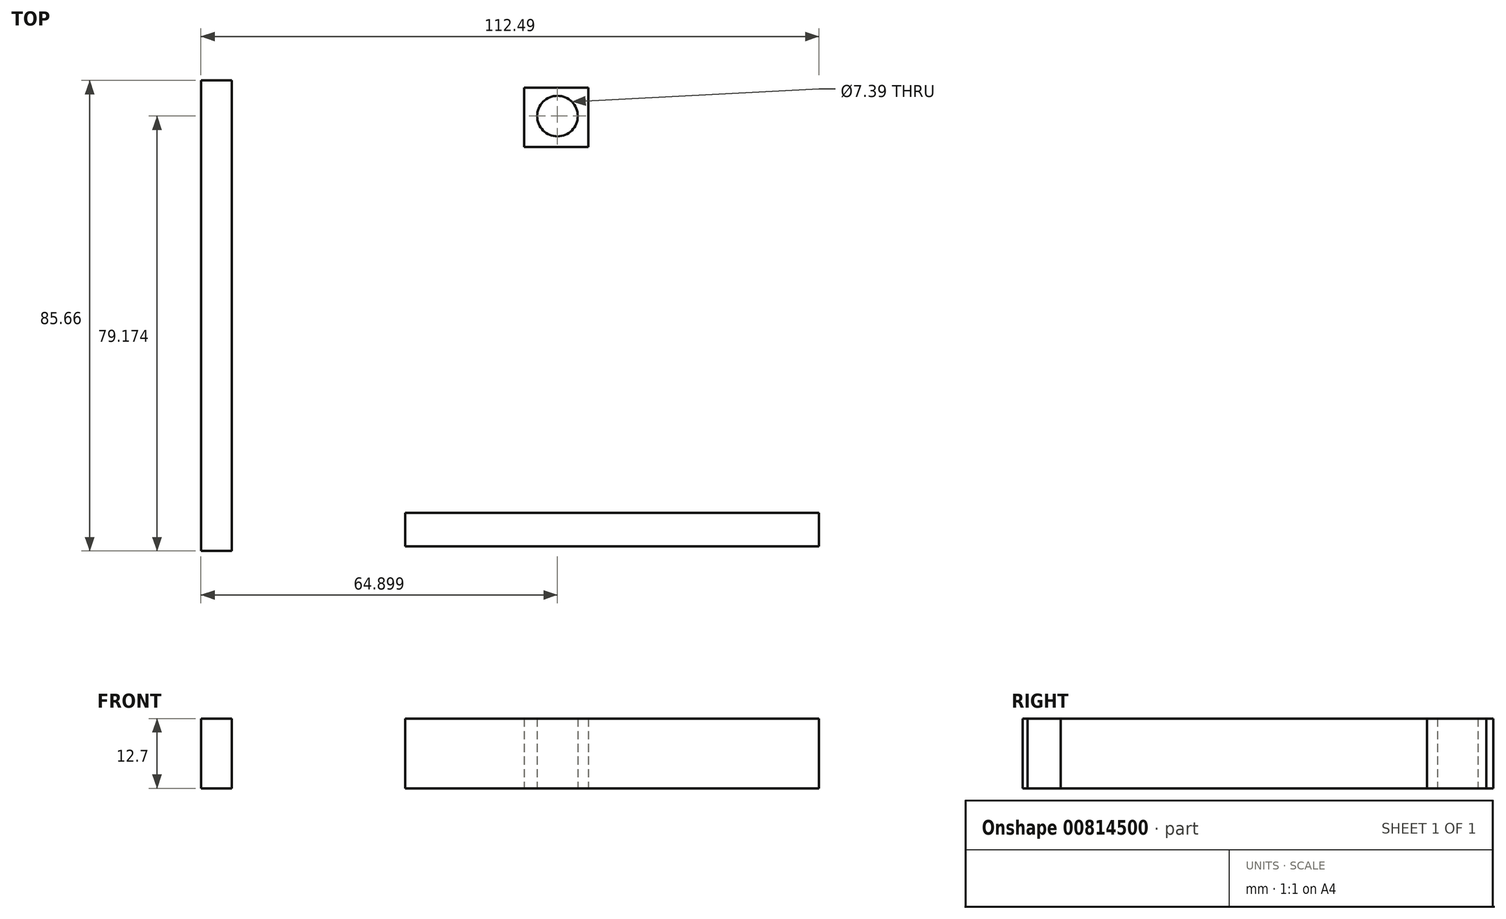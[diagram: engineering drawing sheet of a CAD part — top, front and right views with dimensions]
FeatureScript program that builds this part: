
annotation { "Feature Type Name" : "Feature", "Feature Type Description" : "" }
export const myFeature = defineFeature(function(context is Context, id is Id, definition is map)
    precondition{}
    {
        {
            var Q0;
            Q0=qCreatedBy(makeId("Top.planeOp"),FACE);
            var sketch = newSketch(context, id + "F0", { "sketchPlane" : qUnion([Q0])});
            skLineSegment(sketch, "E0", {"start": v(-31.55, 43.63) * mm, "end": v(-31.55, -42.03) * mm});
            skLineSegment(sketch, "E1", {"start": v(-31.55, -42.03) * mm, "end": v(-37.18, -42.03) * mm});
            skLineSegment(sketch, "E2", {"start": v(-37.18, -42.03) * mm, "end": v(-37.18, 43.63) * mm});
            skLineSegment(sketch, "E3", {"start": v(-37.18, 43.63) * mm, "end": v(-31.55, 43.63) * mm});
            skCircle(sketch, "E4", {"center": v(27.72, 37.14) * mm, "radius": 3.7 * mm});
            skLineSegment(sketch, "E5", {"start": v(21.66, 42.34) * mm, "end": v(21.66, 31.52) * mm});
            skLineSegment(sketch, "E6", {"start": v(21.66, 31.52) * mm, "end": v(33.34, 31.52) * mm});
            skLineSegment(sketch, "E7", {"start": v(21.66, 42.34) * mm, "end": v(33.34, 42.34) * mm});
            skLineSegment(sketch, "E8", {"start": v(33.34, 42.34) * mm, "end": v(33.34, 31.52) * mm});
            skLineSegment(sketch, "E9", {"start": v(0, -41.17) * mm, "end": v(75.31, -41.17) * mm});
            skLineSegment(sketch, "E10", {"start": v(75.31, -41.17) * mm, "end": v(75.31, -35.1) * mm});
            skLineSegment(sketch, "E11", {"start": v(75.31, -35.1) * mm, "end": v(0, -35.1) * mm});
            skLineSegment(sketch, "E12", {"start": v(0, -35.1) * mm, "end": v(0, -41.17) * mm});
            skSolve(sketch);
        }
        {
            var Q0;
            Q0 = qSketchRegion(id + "F0", true);
            extrude(context, id + "F1", {"entities" : qUnion([Q0]), "depth" : 12.7 * mm, "offsetDistance" : 25.4 * mm});
        }
    });
